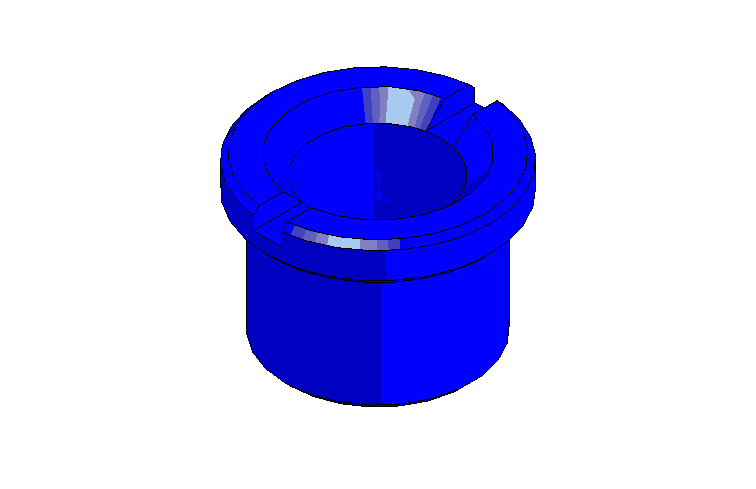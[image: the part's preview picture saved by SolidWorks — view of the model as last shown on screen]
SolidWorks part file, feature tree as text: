
SOLIDWORKS PART (.sldprt)
format: sldprt  version: not decoded by parser v0  size: 192,512 bytes
history: native  units: mm
features: sketch x4, plane x3, extrude x2, cut_extrude x2, chamfer x2, material x1 (+10 scaffold rows collapsed)
feature tree (24):
  scaffold x10  (default folders/planes/origin — collapsed)
  material  "Matériau <non spécifié>"
  plane  "Plan de face"
  plane  "Plan de dessus"
  plane  "Plan de droite"
  sketch  "Esquisse1"  dims[D1=10.0mm]
  extrude  "Extrusion1"  Depth=6.5mm
  sketch  "Esquisse2"  dims[D1=12.0mm]
  extrude  "Extrusion2"  Depth=2mm
  sketch  "Esquisse3"  dims[D1=6.8mm]
  cut_extrude  "Enlèv. mat.-Extru.1"  [1 undecoded]
  chamfer  "Chanfrein1"  Distance=0.3mm Angle=45deg
  chamfer  "Chanfrein2"  Distance=1mm Angle=45deg
  sketch  "Esquisse4"  dims[D1=1.5mm]
  cut_extrude  "Enlèv. mat.-Extru.2"  Depth=1mm
decode coverage: 9 of 10 modeling features carry decoded parameters
note: 1 parameter value undecoded
note: suppression state not decoded; provenance and decode notes live in map.json
